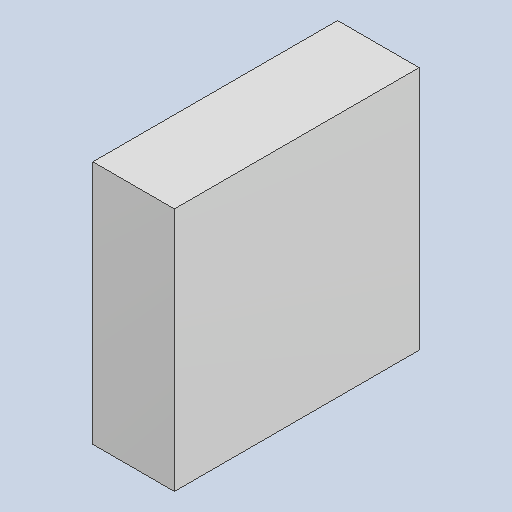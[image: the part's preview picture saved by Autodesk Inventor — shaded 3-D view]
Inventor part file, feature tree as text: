
AUTODESK INVENTOR PART (.ipt)
format: ipt  version: 2023.4 (Build 274418000, 418)  size: 81,408 bytes
history: native  units: mm
features: extrude x1
ambient origin geometry x8: Origin, YZ Plane, XZ Plane, XY Plane, X Axis, Y Axis, Z Axis, Center Point
bodies: Solid1 (feature_tree)
feature tree (1):
  extrude  "Extruded_14"  [1 undecoded]
note: 1 required parameter value undecoded (feature->parameter linkage not recoverable at this tier; creation-order binding heuristic only, values carry confidence <= 0.55)
